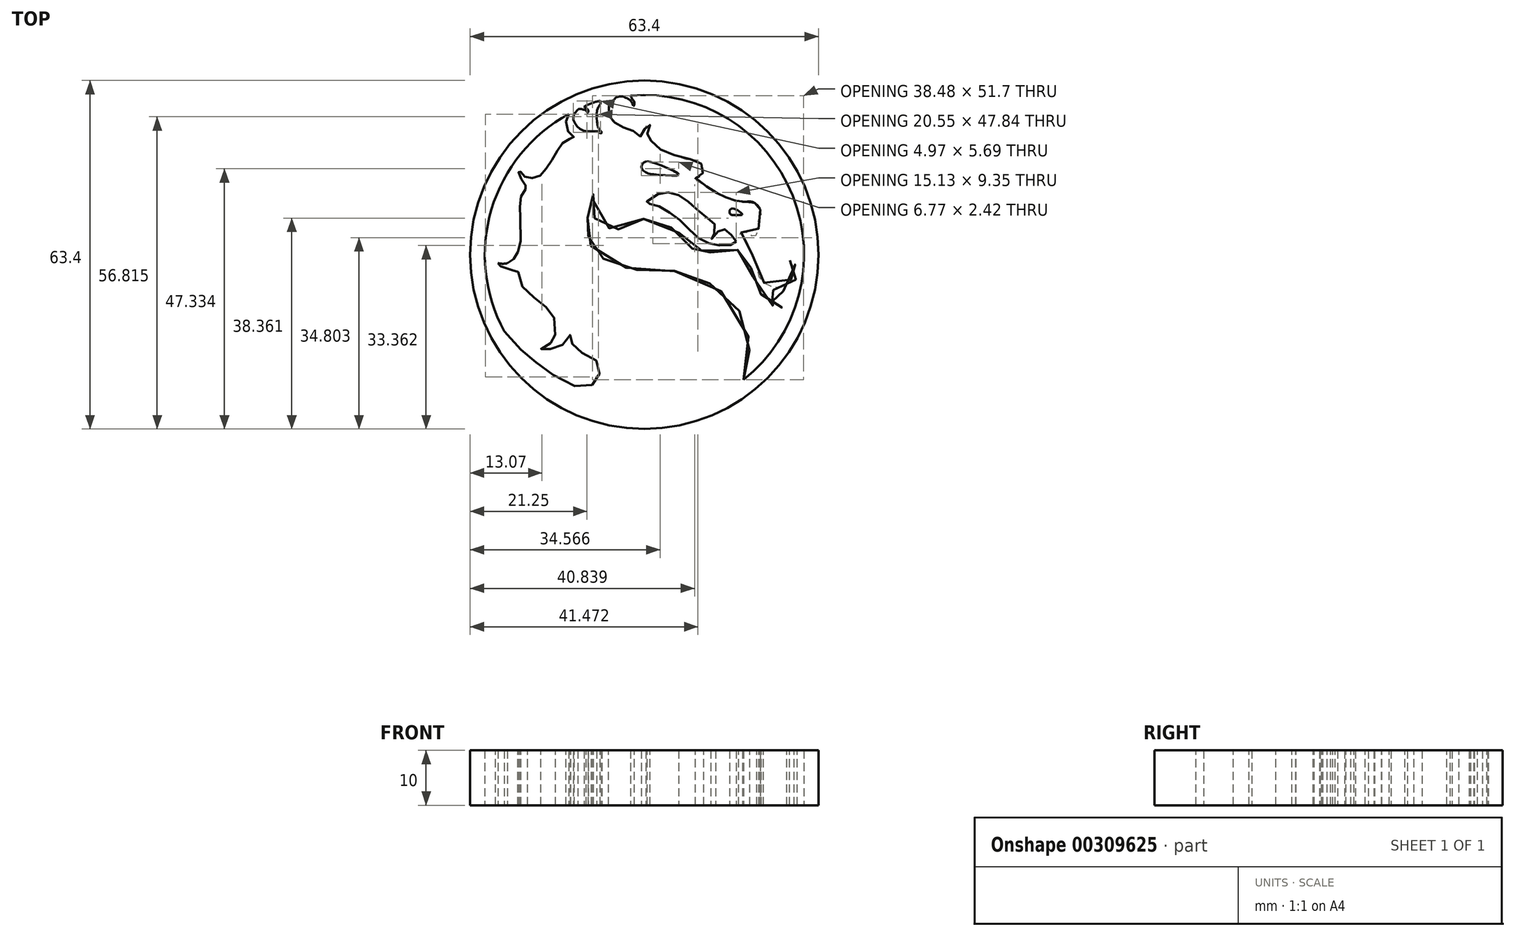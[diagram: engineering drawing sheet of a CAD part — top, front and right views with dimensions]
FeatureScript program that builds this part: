
annotation { "Feature Type Name" : "Feature", "Feature Type Description" : "" }
export const myFeature = defineFeature(function(context is Context, id is Id, definition is map)
    precondition{}
    {
        {
            var Q0;
            Q0=qCreatedBy(makeId("Top.planeOp"),FACE);
            var sketch = newSketch(context, id + "F0", { "sketchPlane" : qUnion([Q0])});
            skCircle(sketch, "E0", {"center": v(0, 0) * mm, "radius": 31.7 * mm});
            skArc(sketch, "E1", {"start": v(-7.96, 27.95) * mm, "mid": v(-9.46, 27.48) * mm, "end": v(-10.93, 26.93) * mm});
            skFitSpline(sketch, "E2", {"points": [v(-25.5, -13.95) * mm, v(-22.7, -17.05) * mm, v(-20.86, -18.67) * mm, v(-18.36, -20.6) * mm, v(-15.95, -22.27) * mm, v(-12.36, -23.98) * mm, v(-10.16, -23.98) * mm, v(-8.94, -23.23) * mm, v(-8.32, -22.18) * mm, v(-8.02, -20.95) * mm, v(-8.32, -19.72) * mm, v(-9.99, -18.54) * mm, v(-11.26, -17.93) * mm, v(-12.22, -17.23) * mm, v(-13.1, -16.26) * mm, v(-13.4, -15.12) * mm, v(-13.4, -14.46) * mm, v(-13.67, -14.9) * mm, v(-14.24, -15.78) * mm, v(-15.03, -16.48) * mm, v(-15.9, -16.96) * mm, v(-17.22, -17.18) * mm, v(-18.06, -17.31) * mm, v(-18.85, -17.31) * mm, v(-18.67, -17.05) * mm, v(-17.88, -16.61) * mm, v(-17.14, -16.13) * mm, v(-16.74, -15.7) * mm, v(-16.52, -15.16) * mm, v(-16.26, -14.6) * mm, v(-16.21, -12.23) * mm, v(-16.54, -11.21) * mm, v(-17.22, -10.16) * mm, v(-18.21, -9.34) * mm, v(-19.41, -8.4) * mm, v(-20.9, -7.06) * mm, v(-22.02, -5.97) * mm, v(-22.84, -4.63) * mm, v(-22.95, -3.05) * mm, v(-22.8, -2.6) * mm, v(-23.37, -2.72) * mm, v(-24.22, -2.82) * mm, v(-25.2, -2.63) * mm, v(-26.25, -2.07) * mm, v(-27.1, -1.5) * mm, v(-27.02, -1.3) * mm, v(-26.62, -1.56) * mm], "startDerivative": vector(73.14, -85.9) * mm, "endDerivative": vector(33.12, -30.6) * mm});
            skArc(sketch, "E3", {"start": v(-26.62, -1.56) * mm, "mid": v(-25.76, -1.65) * mm, "end": v(-24.9, -1.56) * mm});
            skFitSpline(sketch, "E4", {"points": [v(-24.9, -1.56) * mm, v(-24.22, -1.18) * mm, v(-23.58, -0.47) * mm, v(-23.09, 0.44) * mm, v(-22.64, 1.15) * mm, v(-22.61, 7.55) * mm, v(-22.64, 8.78) * mm, v(-22.5, 10.34) * mm, v(-22.04, 11.46) * mm, v(-21.33, 12.17) * mm, v(-21.23, 12.27) * mm, v(-21.7, 12.74) * mm, v(-22.17, 13.42) * mm, v(-22.64, 14.17) * mm, v(-22.87, 14.98) * mm, v(-22.87, 15.55) * mm, v(-22.59, 15.16) * mm, v(-22.12, 14.54) * mm, v(-21.67, 14.15) * mm, v(-20.92, 13.94) * mm, v(-19.85, 14.02) * mm, v(-18.9, 14.46) * mm, v(-18.1, 15.37) * mm, v(-17.27, 16.54) * mm, v(-16.2, 18.27) * mm, v(-15.6, 19.39) * mm, v(-14.82, 20.4) * mm, v(-13.93, 21.03) * mm, v(-12.94, 21.13) * mm, v(-12.76, 21.34) * mm, v(-13.23, 21.6) * mm, v(-13.9, 22.49) * mm, v(-14.24, 24.05) * mm, v(-14, 25.12) * mm, v(-13.7, 25.63) * mm, v(-13.68, 25.64) * mm, v(-13.7, 25.63) * mm], "startDerivative": vector(27.03, 13) * mm, "endDerivative": vector(-4.63, -2.23) * mm});
            skFitSpline(sketch, "E5", {"points": [v(-7.96, 27.95) * mm, v(-7.98, 27.45) * mm, v(-8.51, 26.58) * mm, v(-8.66, 25.66) * mm, v(-8.64, 24.6) * mm, v(-8.59, 23.87) * mm, v(-8.35, 23.06) * mm, v(-8.01, 22.6) * mm, v(-7.74, 22.29) * mm, v(-7.94, 22.07) * mm, v(-8.42, 22.43) * mm, v(-8.9, 22.47) * mm, v(-10.1, 22.45) * mm, v(-11.04, 22.56) * mm, v(-11.98, 23.08) * mm, v(-12.59, 23.82) * mm, v(-12.95, 24.76) * mm, v(-12.72, 25.66) * mm, v(-11.93, 26.5) * mm, v(-11, 26.4) * mm, v(-10.5, 26.12) * mm, v(-10.36, 25.83) * mm, v(-10.19, 26.21) * mm, v(-10.45, 26.55) * mm, v(-10.8, 26.8) * mm, v(-10.93, 26.93) * mm, v(-7.96, 27.95) * mm]});
            skFitSpline(sketch, "E6", {"points": [v(-2.48, 28.95) * mm, v(-2.35, 28.65) * mm, v(-2.13, 28.23) * mm, v(-1.99, 28.1) * mm, v(-1.84, 27.77) * mm, v(-1.9, 27.08) * mm, v(-2.17, 27.53) * mm, v(-2.65, 28.17) * mm, v(-3.07, 28.43) * mm, v(-3.52, 28.61) * mm, v(-3.9, 28.8) * mm, v(-5.2, 28.6) * mm, v(-6, 27.86) * mm, v(-6.43, 27.08) * mm, v(-6.5, 26.48) * mm, v(-6.48, 25.57) * mm, v(-6.28, 25.02) * mm, v(-5.99, 24.56) * mm, v(-5.4, 24.02) * mm, v(-4.7, 23.6) * mm, v(-3.96, 23.23) * mm, v(-3.33, 22.92) * mm, v(-2.48, 22.7) * mm, v(-1.7, 22.35) * mm, v(-1.1, 21.89) * mm, v(-0.75, 21.52) * mm, v(-0.46, 22.2) * mm, v(-0.16, 22.68) * mm, v(0.26, 23.12) * mm, v(0.69, 23.7) * mm, v(1, 23.71) * mm, v(1.02, 23.71) * mm, v(0.96, 23.23) * mm, v(0.72, 22.72) * mm, v(0.56, 21.98) * mm, v(0.72, 21.39) * mm, v(0.94, 21.02) * mm, v(1.38, 20.55) * mm, v(2.37, 19.56) * mm, v(3.61, 18.87) * mm, v(5.26, 18.2) * mm, v(7.33, 17.45) * mm, v(9.38, 17.26) * mm, v(10.03, 16.9) * mm, v(10.74, 15.96) * mm, v(10.78, 15.4) * mm, v(10.53, 14.66) * mm, v(9.97, 14.25) * mm, v(9.57, 14) * mm, v(9.29, 13.82) * mm, v(10.76, 12.74) * mm, v(12.49, 11.67) * mm, v(13.12, 11.27) * mm, v(13.74, 10.96) * mm, v(14.4, 10.7) * mm, v(15.2, 10.29) * mm, v(16.17, 9.97) * mm, v(16.86, 9.8) * mm, v(17.82, 9.66) * mm, v(18.56, 9.64) * mm, v(19.11, 9.7) * mm, v(19.73, 9.59) * mm, v(20.34, 9.22) * mm, v(20.81, 8.74) * mm, v(21.1, 8.24) * mm, v(21.09, 8.23) * mm], "startDerivative": vector(11.35, -25.78) * mm, "endDerivative": vector(-1.39, -4.3) * mm});
            skFitSpline(sketch, "E7", {"points": [v(21.1, 8.23) * mm, v(21.3, 7.6) * mm, v(20.78, 6.66) * mm, v(20.5, 6.47) * mm, v(20.73, 6.03) * mm, v(20.84, 5.17) * mm, v(20.42, 3.7) * mm, v(19.9, 3.18) * mm, v(19.43, 3.6) * mm, v(18.65, 3.98) * mm, v(17.69, 4.04) * mm, v(17.2, 3.96) * mm, v(17.87, 3.36) * mm, v(18.64, 2.35) * mm, v(19.33, 0.75) * mm, v(20, -0.85) * mm, v(20.52, -2.6) * mm, v(21.1, -4.44) * mm, v(22.36, -5.44) * mm, v(23.93, -5.93) * mm, v(25.25, -5.72) * mm, v(26.43, -4.89) * mm, v(27.16, -3.5) * mm, v(27.1, -2.17) * mm, v(26.47, -1.03) * mm, v(27.2, -1.48) * mm, v(27.8, -2.9) * mm, v(27.55, -4.57) * mm, v(26.36, -6.07) * mm, v(24.24, -6.66) * mm, v(21.77, -6.04) * mm, v(22.3, -7.53) * mm, v(24.03, -8.79) * mm, v(25.7, -9.27) * mm, v(25.95, -9.48) * mm, v(24.62, -9.59) * mm, v(22.85, -8.96) * mm, v(21.5, -7.57) * mm, v(20.27, -5.51) * mm, v(19.61, -3.29) * mm, v(18.88, -0.78) * mm, v(17.77, 1.17) * mm, v(16.69, 0.65) * mm, v(14.22, -0.26) * mm, v(11.82, 0.5) * mm, v(10.08, 0.68) * mm, v(9.17, 0.37) * mm, v(8.69, 1.27) * mm, v(6.84, 3.57) * mm, v(4.86, 4.96) * mm, v(2.28, 6.42) * mm, v(0, 6.56) * mm, v(-2.42, 5.7) * mm, v(-4.16, 4.75) * mm, v(-6.28, 4.79) * mm, v(-8.33, 5.8) * mm, v(-9.44, 7.64) * mm, v(-9.44, 10.32) * mm, v(-9.24, 11.02) * mm, v(-9.97, 10.11) * mm, v(-10.56, 8.23) * mm, v(-10.04, 6.21) * mm, v(-9.37, 5.38) * mm, v(-9.86, 4.82) * mm, v(-10.07, 2.63) * mm, v(-9.1, 0.71) * mm, v(-7.29, -0.82) * mm, v(-3.42, -2.35) * mm, v(-0.43, -2.8) * mm, v(4.1, -2.8) * mm, v(8.3, -3.67) * mm, v(12.06, -5.3) * mm, v(15.89, -8.5) * mm, v(18.4, -12.47) * mm, v(19.16, -17.42) * mm, v(18.9, -20.57) * mm, v(18.08, -22.75) * mm, v(18.05, -22.78) * mm], "startDerivative": vector(44.78, -70.7) * mm, "endDerivative": vector(-14.23, -4.64) * mm});
            skPoint(sketch, "E8", {"position": v(-12.1, 26.41) * mm});
            skPoint(sketch, "E9", {"position": v(-11.83, 26.52) * mm});
            skPoint(sketch, "E10", {"position": v(-13.74, 25.58) * mm});
            skFitSpline(sketch, "E11.trimOffspring", {"points": [v(-2.48, 28.95) * mm, v(-2.35, 28.65) * mm, v(-2.13, 28.23) * mm, v(-1.99, 28.1) * mm, v(-1.84, 27.77) * mm, v(-1.9, 27.08) * mm, v(-2.17, 27.53) * mm, v(-2.65, 28.17) * mm, v(-3.07, 28.43) * mm, v(-3.52, 28.61) * mm, v(-3.9, 28.8) * mm, v(-5.2, 28.6) * mm, v(-6, 27.86) * mm, v(-6.43, 27.08) * mm, v(-6.5, 26.48) * mm, v(-6.48, 25.57) * mm, v(-6.28, 25.02) * mm, v(-5.99, 24.56) * mm, v(-5.4, 24.02) * mm, v(-4.7, 23.6) * mm, v(-3.96, 23.23) * mm, v(-3.33, 22.92) * mm, v(-2.48, 22.7) * mm, v(-1.7, 22.35) * mm, v(-1.1, 21.89) * mm, v(-0.75, 21.52) * mm, v(-0.46, 22.2) * mm, v(-0.16, 22.68) * mm, v(0.26, 23.12) * mm, v(0.69, 23.7) * mm, v(1, 23.71) * mm, v(1.02, 23.71) * mm, v(0.96, 23.23) * mm, v(0.72, 22.72) * mm, v(0.56, 21.98) * mm, v(0.72, 21.39) * mm, v(0.94, 21.02) * mm, v(1.38, 20.55) * mm, v(2.37, 19.56) * mm, v(3.61, 18.87) * mm, v(5.26, 18.2) * mm, v(7.33, 17.45) * mm, v(9.38, 17.26) * mm, v(10.03, 16.9) * mm, v(10.74, 15.96) * mm, v(10.78, 15.4) * mm, v(10.53, 14.66) * mm, v(9.97, 14.25) * mm, v(9.57, 14) * mm, v(9.29, 13.82) * mm, v(10.76, 12.74) * mm, v(12.49, 11.67) * mm, v(13.12, 11.27) * mm, v(13.74, 10.96) * mm, v(14.4, 10.7) * mm, v(15.2, 10.29) * mm, v(16.17, 9.97) * mm, v(16.86, 9.8) * mm, v(17.82, 9.66) * mm, v(18.56, 9.64) * mm, v(19.11, 9.7) * mm, v(19.73, 9.59) * mm, v(20.34, 9.22) * mm, v(20.81, 8.74) * mm, v(21.1, 8.24) * mm, v(21.09, 8.23) * mm], "startDerivative": vector(11.35, -25.78) * mm, "endDerivative": vector(-1.39, -4.3) * mm});
            skArc(sketch, "E12.trimOffspring", {"start": v(-3.9, 28.8) * mm, "mid": v(-4.55, 28.7) * mm, "end": v(-5.2, 28.6) * mm});
            skArc(sketch, "E13.trimOffspring", {"start": v(18.08, -22.75) * mm, "mid": v(27, 10.74) * mm, "end": v(-2.48, 28.95) * mm});
            skLineSegment(sketch, "E14", {"start": v(-12.1, 26.41) * mm, "end": v(-11.83, 26.52) * mm});
            skArc(sketch, "E15", {"start": v(-13.74, 25.58) * mm, "mid": v(-27.82, 8.25) * mm, "end": v(-25.5, -13.95) * mm});
            skFitSpline(sketch, "E16", {"points": [v(6.25, 14.54) * mm, v(1.57, 16.78) * mm, v(0, 16.86) * mm, v(-0.56, 15.95) * mm, v(0, 15.19) * mm, v(0.58, 14.82) * mm, v(1.46, 14.68) * mm, v(6.25, 14.54) * mm]});
            skFitSpline(sketch, "E17", {"points": [v(17.84, 7.32) * mm, v(16.29, 8.38) * mm, v(15.53, 8) * mm, v(15.76, 7.32) * mm, v(17.3, 7.25) * mm, v(17.84, 7.32) * mm]});
            skFitSpline(sketch, "E18", {"points": [v(16.7, 2.4) * mm, v(16.25, 1.91) * mm, v(14.28, 1.65) * mm, v(12, 1.99) * mm, v(9.66, 3.16) * mm, v(7.2, 5.58) * mm, v(4.78, 7.55) * mm, v(2.35, 8.95) * mm, v(0.73, 9.25) * mm, v(0.27, 9.4) * mm, v(2.43, 11) * mm, v(4.44, 11.34) * mm, v(6.7, 10.62) * mm, v(9.02, 8.76) * mm, v(11.36, 6.72) * mm, v(12.69, 5.73) * mm, v(12.8, 3.92) * mm, v(12.12, 3) * mm, v(12.5, 2.93) * mm, v(13.9, 4.83) * mm, v(14.92, 4.4) * mm, v(16.06, 3.39) * mm, v(16.7, 2.4) * mm]});
            skSolve(sketch);
        }
        {
            var Q0;
            Q0=qSketchRegion(id+"F0",true);
            extrude(context, id + "F1", {"entities" : qUnion([Q0]), "depth" : 10 * mm});
        }
    });
